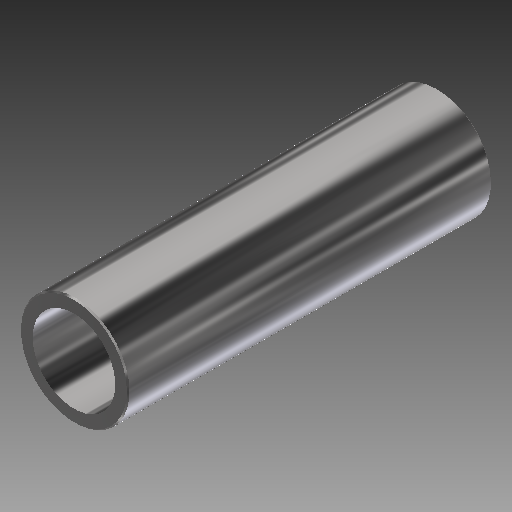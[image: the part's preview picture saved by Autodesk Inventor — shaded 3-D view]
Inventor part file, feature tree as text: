
AUTODESK INVENTOR PART (.ipt)
format: ipt  version: 2018 (Build 220112000, 112)  size: 179,712 bytes
history: native  units: in
note: dims shown in document units (in); Inventor stores cm internally (conversion verified against a paired STEP export)
features: other x21, revolve x1, sketch x1
ambient origin geometry x8: Origin, YZ Plane, XZ Plane, XY Plane, X Axis, Y Axis, Z Axis, Center Point
bodies: Solid1 (feature_tree)
feature tree (23):
  revolve  "Revolution1"  [1 undecoded]
  other  "cap_XY"
  other  "cap_YZ"
  other  "cap_ZX"
  other  "cap_X"
  other  "cap_Y"
  other  "cap_Z"
  other  "cap_Center"
  other  "ctr_XY"
  other  "ctr_YZ"
  other  "ctr_ZX"
  other  "ctr_X"
  other  "ctr_Y"
  other  "ctr_Z"
  other  "ctr_Center"
  other  "hd_XY"
  other  "hd_YZ"
  other  "hd_ZX"
  other  "hd_X"
  other  "hd_Y"
  other  "hd_Z"
  other  "hd_Center"
  sketch  "Sketch_2"  dims[d0=360.0deg d1=0.0in d2=0.0in]
note: 1 required parameter value undecoded (feature->parameter linkage not recoverable at this tier; creation-order binding heuristic only, values carry confidence <= 0.55)
